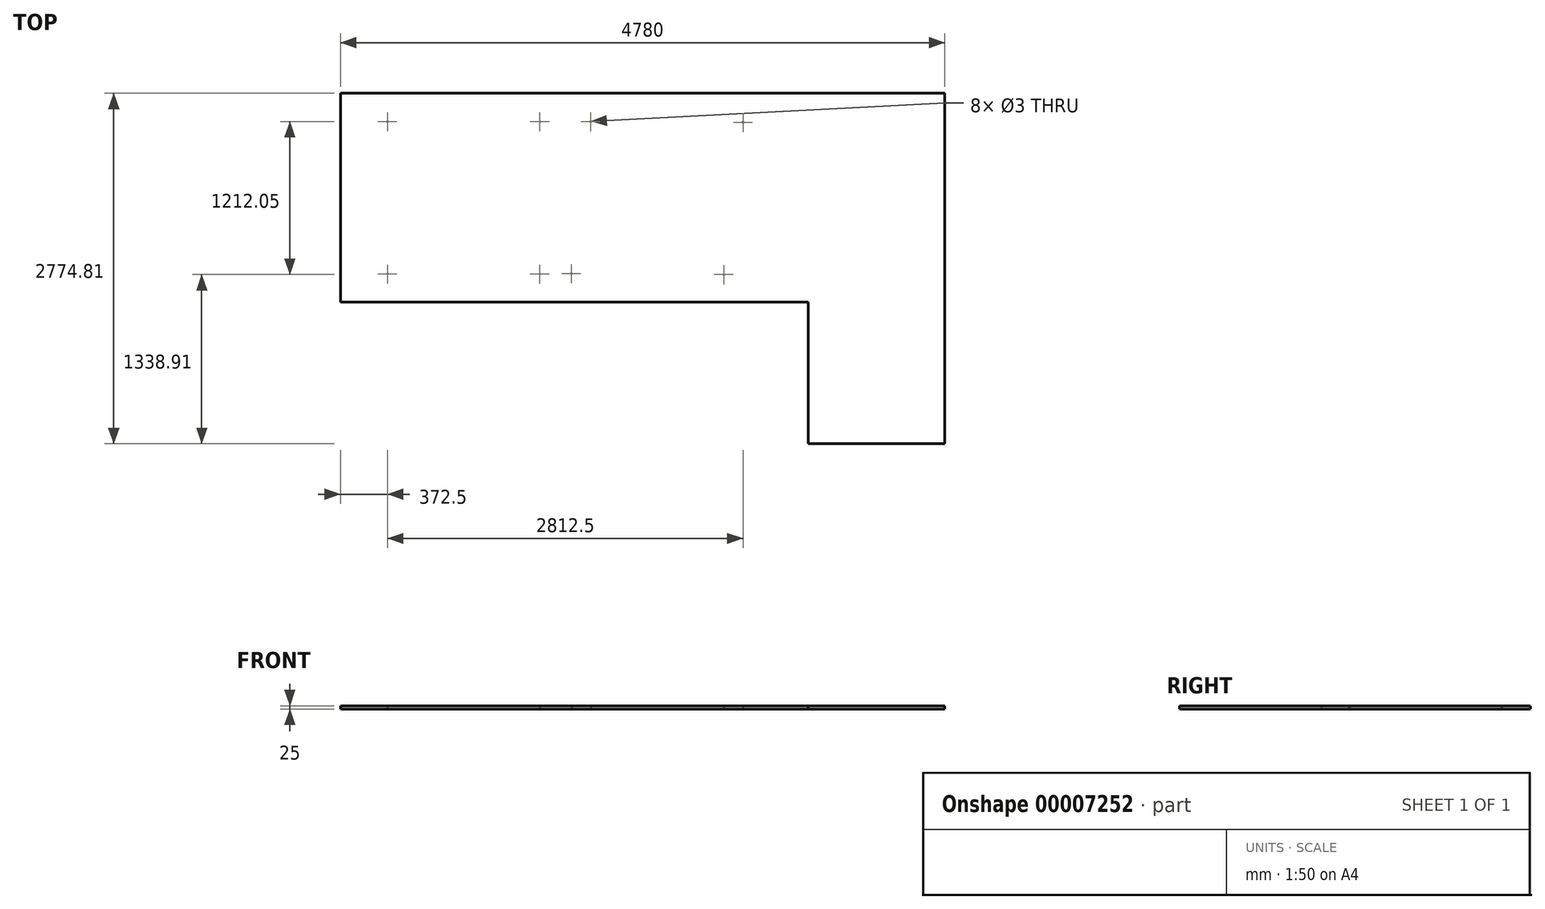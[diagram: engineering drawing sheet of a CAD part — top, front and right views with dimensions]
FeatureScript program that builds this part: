
annotation { "Feature Type Name" : "Feature", "Feature Type Description" : "" }
export const myFeature = defineFeature(function(context is Context, id is Id, definition is map)
    precondition{}
    {
        {
            var Q0;
            Q0=qCreatedBy(makeId("Top.planeOp"),FACE);
            var sketch = newSketch(context, id + "F0", { "sketchPlane" : qUnion([Q0])});
            skLineSegment(sketch, "E0.0", {"start": v(4942.46, 1189.43) * mm, "end": v(4942.46, -1585.38) * mm});
            skLineSegment(sketch, "E0.1", {"start": v(162.46, 1189.43) * mm, "end": v(4942.46, 1189.43) * mm});
            skLineSegment(sketch, "E0.2", {"start": v(162.46, -465.57) * mm, "end": v(162.46, 1189.43) * mm});
            skLineSegment(sketch, "E0.3", {"start": v(3862.46, -465.57) * mm, "end": v(162.46, -465.57) * mm});
            skLineSegment(sketch, "E0.4", {"start": v(3862.46, -1585.38) * mm, "end": v(3862.46, -465.57) * mm});
            skLineSegment(sketch, "E1", {"start": v(3862.46, -1585.38) * mm, "end": v(4942.46, -1585.38) * mm});
            skCircle(sketch, "E2", {"center": v(534.96, -240.57) * mm, "radius": 1.5 * mm});
            skCircle(sketch, "E3.1.0", {"center": v(1739.96, -240.57) * mm, "radius": 1.5 * mm});
            skCircle(sketch, "E3.2.0", {"center": v(1739.96, 964.43) * mm, "radius": 1.5 * mm});
            skCircle(sketch, "E3.3.0", {"center": v(534.96, 964.43) * mm, "radius": 1.5 * mm});
            skPoint(sketch, "E3.center", {"position": v(1137.46, 361.93) * mm});
            skCircle(sketch, "E4", {"center": v(1989.96, -239.42) * mm, "radius": 1.5 * mm});
            skCircle(sketch, "E5", {"center": v(2142.46, 965.58) * mm, "radius": 1.5 * mm});
            skCircle(sketch, "E6", {"center": v(3347.46, 958.53) * mm, "radius": 1.5 * mm});
            skCircle(sketch, "E7", {"center": v(3194.96, -246.47) * mm, "radius": 1.5 * mm});
            skSolve(sketch);
        }
        {
            var Q0;
            Q0=makeQuery(id+"F0.imprint","IMPRINT",FACE,{"disambiguationData":[TD([[makeQuery(id+"F0.imprint","IMPRINT",EDGE,{"derivedFrom":sQuery(id+"F0.wireOp",EDGE,"E0.0")}),-1.0]])]});
            extrude(context, id + "F1", {"entities" : qUnion([Q0]), "depth" : 25 * mm});
        }
    });
